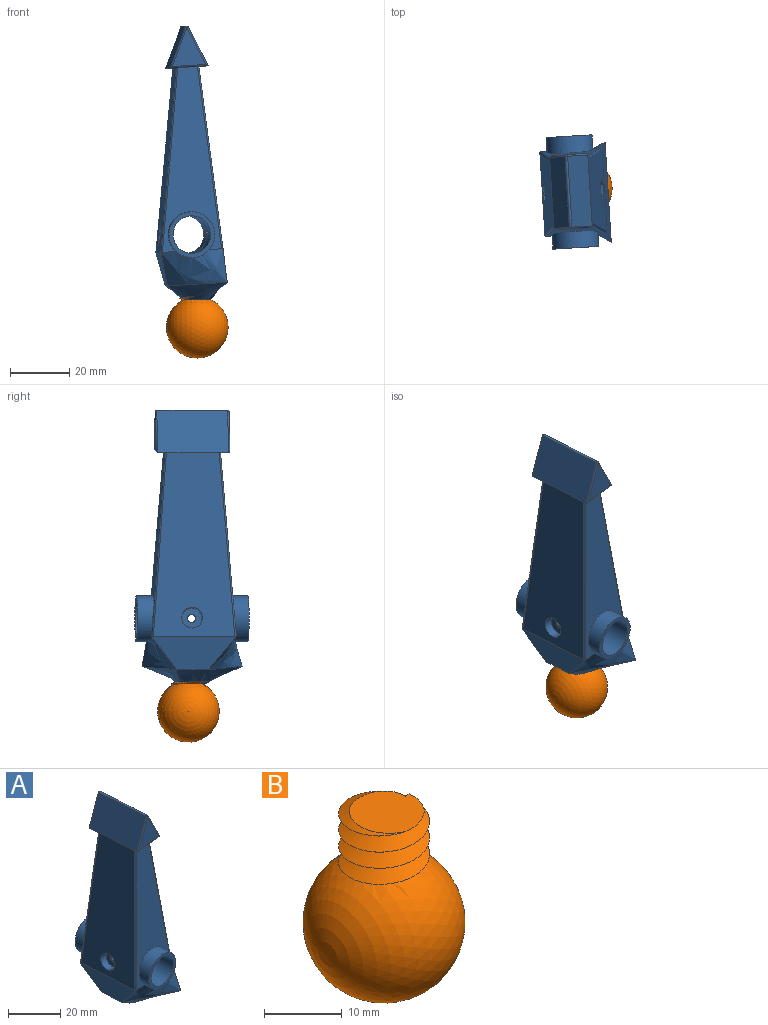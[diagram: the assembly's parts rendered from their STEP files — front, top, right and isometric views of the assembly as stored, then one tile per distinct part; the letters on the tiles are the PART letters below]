
ASSEMBLY  parts=2 mates=1
PART A: 59 faces, bbox 27x39.9x94.6 mm
  f0: bspline ~20.3x14.82mm, area 124.5mm2, adj f1,f7,f18,f19,f21,f49,f50,f56
  f1: bspline ~10.74x7.54mm, area 62.6mm2, adj f0,f17,f20,f50
  f2: cylinder r=3.87mm len=12.03mm, axis (0.06,0,-1), area 202.6mm2, adj f3,f5,f43,f50,f55
  f3: cylinder r=3.87mm len=2.24mm, axis (0.06,0,-1), area 0.6mm2, adj f2,f49,f50,f51,f54
  f4: plane 61.62x28.53mm, normal (0.99,0.06,0.13), area 1371.3mm2, adj f6,f7,f9,f16,f22,f23,f42,f43
  f5: cylinder r=6.35mm len=38.48mm, axis (-0.06,1,0), area 1405.3mm2, adj f2,f35,f38,f41,f42,f43,f44,f45
  f6: bspline ~23.66x18.17mm, area 242.5mm2, adj f4,f15,f16,f17,f20,f22,f25,f36
  f7: bspline ~22.85x15.03mm, area 247.7mm2, adj f0,f4,f14,f16,f17,f23,f24,f37
  f8: plane 24.26x13.91mm, normal (-0.93,-0.06,0.35), area 356.3mm2, adj f9,f29,f30,f34
  f9: plane 24.78x14.47mm, normal (0.06,0,-1), area 167.1mm2, adj f4,f8,f10,f13,f14,f15,f22,f23
  f10: plane 24.36x13.19mm, normal (0.89,0.05,0.46), area 356.3mm2, adj f9,f28,f31,f34
  f11: plane 13.18x11.39mm, normal (0.06,-1,0), area 73.5mm2, adj f26,f28,f29
  f12: plane 13.18x11.39mm, normal (-0.06,1,0), area 73.5mm2, adj f27,f30,f31
  f13: plane 62.41x27.52mm, normal (-0.99,-0.06,0.09), area 1383.1mm2, adj f9,f17,f24,f25,f39
  f14: plane 62.81x19.96mm, normal (0.06,-1,0.08), area 659.2mm2, adj f7,f9,f23,f24,f37
  f15: plane 62.81x19.96mm, normal (-0.07,0.99,0.08), area 658.9mm2, adj f6,f9,f22,f25,f36
  f16: bspline ~33.83x11.38mm, area 357.5mm2, adj f4,f6,f7,f21
  f17: plane 28.25x11.42mm, normal (-0.97,-0.06,-0.23), area 228.1mm2, adj f1,f6,f7,f13,f24,f25
  f18: plane 9.38x5.23mm, normal (0.06,0,-1), area 8.3mm2, adj f0,f20,f21,f48,f50,f56
  f19: bspline ~6.46x5.78mm, area 0mm2, adj f0,f49,f56
  f20: bspline ~18.88x14.1mm, area 123.6mm2, adj f1,f6,f18,f21,f50
  f21: bspline ~33.83x7.49mm, area 158.5mm2, adj f0,f16,f18,f20
  f22: cylinder r=0.51mm len=61.66mm, axis (-0.12,-0.08,0.99), area 47.3mm2, adj f4,f6,f9,f15
  f23: cylinder r=0.51mm len=61.66mm, axis (0.13,-0.07,-0.99), area 48.6mm2, adj f4,f7,f9,f14
  f24: cylinder r=0.51mm len=62.73mm, axis (0.08,0.08,0.99), area 49.9mm2, adj f7,f9,f13,f14,f17
  f25: cylinder r=0.51mm len=62.75mm, axis (-0.09,0.07,-0.99), area 49.9mm2, adj f6,f9,f13,f15,f17
  f26: cylinder r=0.51mm len=12.97mm, axis (-1,-0.06,-0.06), area 9.7mm2, adj f9,f11,f28,f29
  f27: cylinder r=0.51mm len=13.01mm, axis (1,0.06,0.06), area 9.7mm2, adj f9,f12,f30,f31
  f28: cylinder r=0.51mm len=13.43mm, axis (0.46,0.03,-0.89), area 11.5mm2, adj f10,f11,f26,f32
  f29: cylinder r=0.51mm len=14.09mm, axis (0.35,0.02,0.94), area 11.5mm2, adj f8,f11,f26,f32
  f30: cylinder r=0.51mm len=14.09mm, axis (-0.35,-0.02,-0.94), area 11.5mm2, adj f8,f12,f27,f33
  f31: cylinder r=0.51mm len=13.43mm, axis (-0.46,-0.03,0.89), area 11.5mm2, adj f10,f12,f27,f33
  f32: sphere r=0.51mm, area 0.6mm2, adj f28,f29,f34
  f33: sphere r=0.51mm, area 0.6mm2, adj f30,f31,f34
  f34: cylinder r=0.51mm len=24mm, axis (-0.06,1,0), area 28.1mm2, adj f8,f10,f32,f33
  f35: plane 15.53x15.5mm, normal (-0.06,1,0), area 62.7mm2, adj f5,f36
  f36: cylinder r=7.76mm len=15.85mm, axis (-0.06,1,0), area 250mm2, adj f6,f15,f35
  f37: cylinder r=7.76mm len=15.84mm, axis (-0.06,1,0), area 242.5mm2, adj f7,f14,f38
  f38: plane 15.53x15.5mm, normal (0.06,-1,0), area 62.7mm2, adj f5,f37
  f39: cylinder r=3.51mm len=7.27mm, axis (-0.99,-0.06,0.09), area 70mm2, adj f13,f40
  f40: plane 7.01x6.99mm, normal (-0.99,-0.06,0.09), area 33mm2, adj f39,f41
  f41: cylinder r=1.35mm len=2.72mm, axis (-0.99,-0.06,0.09), area 1.6mm2, adj f5,f40
  f42: plane 4.69x4.04mm, normal (-0.12,0.86,0.5), area 15.9mm2, adj f4,f5,f43,f47
  f43: plane 4.86x4.21mm, normal (-0.13,-0.01,0.99), area 18.2mm2, adj f2,f4,f5,f42,f44
  f44: plane 4.69x4.04mm, normal (-0.01,-0.87,0.5), area 15.9mm2, adj f4,f5,f43,f45
  f45: plane 5.2x3.9mm, normal (0.12,-0.86,-0.5), area 16.3mm2, adj f4,f5,f44,f46
  f46: plane 5.09x4.22mm, normal (0.13,0.01,-0.99), area 19.2mm2, adj f4,f5,f45,f47
  f47: plane 5.44x3.9mm, normal (0.01,0.87,-0.5), area 16.3mm2, adj f4,f5,f42,f46
  f48: cylinder r=3.87mm len=7.35mm, axis (0.06,0,-1), area 5.8mm2, adj f18,f49,f50,f53,f56
  f49: bspline ~13.51x11.7mm, area 214.8mm2, adj f0,f3,f19,f48,f50,f51,f52,f53
  f50: bspline ~11.68x11.68mm, area 223.9mm2, adj f0,f1,f2,f3,f18,f20,f48,f49
  f51: cylinder r=3.87mm len=7.32mm, axis (0,0,-1), area 3.5mm2, adj f3,f49,f50,f57
  f52: cylinder r=3.87mm len=7.55mm, axis (0,0,-1), area 3.2mm2, adj f49,f50,f57,f58
  f53: cylinder r=3.87mm len=7.66mm, axis (0,0,-1), area 3.2mm2, adj f48,f49,f50,f58
  f54: plane 0.66x0.37mm, normal (0,-1,0), area 0.1mm2, adj f3,f49,f55
  f55: plane 10.9x10.88mm, normal (0,0,-1), area 24.2mm2, adj f2,f49,f50,f54
  f56: sphere r=10.41mm, area 2.8mm2, adj f0,f18,f19,f48,f49
  f57: cylinder r=3.87mm len=7.49mm, axis (0.06,0,-1), area 6.5mm2, adj f49,f50,f51,f52
  f58: cylinder r=3.87mm len=7.66mm, axis (0.06,0,-1), area 7.1mm2, adj f49,f50,f52,f53
PART B: 6 faces, bbox 21.4x21.4x30.4 mm
  f0: bspline ~13.51x11.7mm, area 240mm2, adj f1,f2,f3,f4,f5
  f1: bspline ~13.51x11.7mm, area 241.9mm2, adj f0,f2,f4,f5
  f2: cylinder r=3.87mm len=8.26mm, axis (0,0,-1), area 20.4mm2, adj f0,f1,f3,f4,f5
  f3: plane 0.67x0.39mm, normal (0,1,0), area 0.1mm2, adj f0,f2,f5
  f4: sphere r=10.41mm, area 1286.1mm2, adj f0,f1,f2
  f5: plane 10.24x10.21mm, normal (0,0,1), area 71mm2, adj f0,f1,f2,f3
PLACE A t=(-45.62,4.91,-7.34)mm
PLACE B t=(-45.29,5.86,-7.34)mm
MATE revolute B.f5 <-> A.f55  axis (0,0,1) through (-45.62,5,10.58)mm
